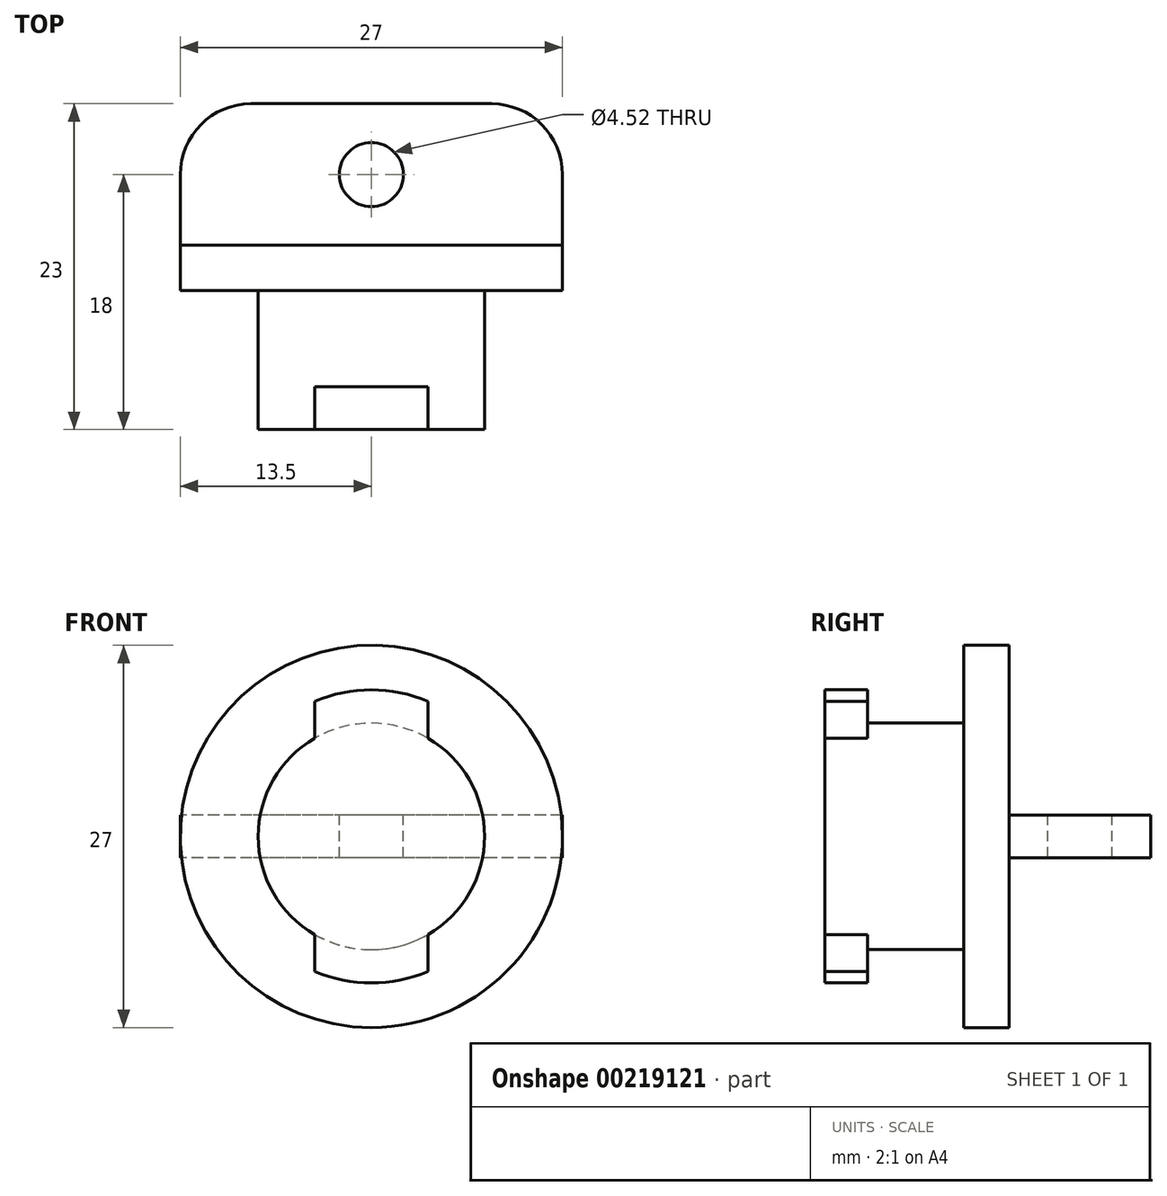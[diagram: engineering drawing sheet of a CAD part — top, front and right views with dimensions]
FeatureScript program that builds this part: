
annotation { "Feature Type Name" : "Feature", "Feature Type Description" : "" }
export const myFeature = defineFeature(function(context is Context, id is Id, definition is map)
    precondition{}
    {
        {
            var Q0;
            Q0=qCreatedBy(makeId("Front.planeOp"),FACE);
            var sketch = newSketch(context, id + "F0", { "sketchPlane" : qUnion([Q0])});
            skCircle(sketch, "E0", {"center": v(0, 0) * mm, "radius": 13.5 * mm});
            skCircle(sketch, "E1", {"center": v(0, 0) * mm, "radius": 8 * mm});
            skSolve(sketch);
        }
        {
            var Q0;
            Q0=makeQuery(id+"F0.imprint","IMPRINT",FACE,{"disambiguationData":[TD([[makeQuery(id+"F0.imprint","IMPRINT",EDGE,{"derivedFrom":sQuery(id+"F0.wireOp",EDGE,"E1")}),1.0]])]});
            extrude(context, id + "F1", {"entities" : qUnion([Q0]), "depth" : 13 * mm});
        }
        {
            var Q0;
            Q0=qSketchRegion(id+"F0",true);
            extrude(context, id + "F2", {"entities" : qUnion([Q0]), "operationType" : NewBodyOperationType.ADD, "depth" : 3.2 * mm});
        }
        {
            var Q0;
            Q0=makeQuery(id+"F2.opExtrude","CAP_FACE",FACE,{"disambiguationData":[OSD([sQuery(id+"F0.wireOp",EDGE,"E0"),sQuery(id+"F0.wireOp",EDGE,"E1")])],"isStart":false});
            cPlane(context, id + "F3", {"entities" : qUnion([Q0]), "cplaneType" : CPlaneType.OFFSET, "offset" : 6.8 * mm, "width" : 150 * mm, "height" : 150 * mm});
        }
        {
            var Q0;
            Q0=qCreatedBy(id+"F3.planeOp",FACE);
            var sketch = newSketch(context, id + "F4", { "sketchPlane" : qUnion([Q0])});
            skLineSegment(sketch, "E2.bottom", {"start": v(4, -10.35) * mm, "end": v(-4, -10.35) * mm});
            skLineSegment(sketch, "E2.top", {"start": v(4, 10.35) * mm, "end": v(-4, 10.35) * mm});
            skLineSegment(sketch, "E2.left", {"start": v(4, -10.35) * mm, "end": v(4, 10.35) * mm});
            skLineSegment(sketch, "E2.right", {"start": v(-4, -10.35) * mm, "end": v(-4, 10.35) * mm});
            skPoint(sketch, "E2.middle", {"position": v(0, 0) * mm});
            skCircle(sketch, "E3", {"center": v(0, 0) * mm, "radius": 10.35 * mm});
            skSolve(sketch);
        }
        {
            var Q0;
            {var subQ0=sQuery(id+"F4.wireOp",EDGE,"E3");var subQ5=sQuery(id+"F4.wireOp",EDGE,"E2.left");var subQ6=makeQuery(id+"F4.imprint","INTERSECT",VERTEX,{"disambiguationData":[OD(0.0)],"derivedFrom":[subQ5,subQ0]});Q0=makeQuery(id+"F4.imprint","IMPRINT",FACE,{"disambiguationData":[TD([[makeQuery(id+"F4.imprint","IMPRINT",EDGE,{"disambiguationData":[TD([[subQ6,-1.0]])],"derivedFrom":subQ5}),1.0]])]});}
            extrude(context, id + "F5", {"entities" : qUnion([Q0]), "operationType" : NewBodyOperationType.ADD, "depth" : 3 * mm});
        }
        {
            var Q0;
            Q0=qCreatedBy(makeId("Front.planeOp"),FACE);
            var sketch = newSketch(context, id + "F6", { "sketchPlane" : qUnion([Q0])});
            skLineSegment(sketch, "E4.bottom", {"start": v(13.5, -1.5) * mm, "end": v(-13.5, -1.5) * mm});
            skLineSegment(sketch, "E4.top", {"start": v(13.5, 1.5) * mm, "end": v(-13.5, 1.5) * mm});
            skLineSegment(sketch, "E4.left", {"start": v(13.5, -1.5) * mm, "end": v(13.5, 1.5) * mm});
            skLineSegment(sketch, "E4.right", {"start": v(-13.5, -1.5) * mm, "end": v(-13.5, 1.5) * mm});
            skPoint(sketch, "E4.middle", {"position": v(0, 0) * mm});
            skSolve(sketch);
        }
        {
            var Q0;
            Q0=makeQuery(id+"F6.imprint","IMPRINT",FACE,{"disambiguationData":[TD([[makeQuery(id+"F6.imprint","IMPRINT",EDGE,{"derivedFrom":sQuery(id+"F6.wireOp",EDGE,"E4.bottom")}),-1.0]])]});
            extrude(context, id + "F7", {"entities" : qUnion([Q0]), "operationType" : NewBodyOperationType.ADD, "oppositeDirection" : true, "depth" : 10 * mm});
        }
        {
            var Q0;
            Q0=makeQuery(id+"F7.opExtrude","CAP_EDGE",EDGE,{"disambiguationData":[OSD([sQuery(id+"F6.wireOp",EDGE,"E4.right")])],"isStart":false});
            fillet(context, id + "F8", {"entities" : qUnion([Q0]), "radius" : 5 * mm, "tangentPropagation" : true, "allowEdgeOverflow" : false});
        }
        {
            var Q0;
            Q0=makeQuery(id+"F7.opExtrude","CAP_EDGE",EDGE,{"disambiguationData":[OSD([sQuery(id+"F6.wireOp",EDGE,"E4.left")])],"isStart":false});
            fillet(context, id + "F9", {"entities" : qUnion([Q0]), "radius" : 5 * mm, "tangentPropagation" : true, "allowEdgeOverflow" : false});
        }
        {
            var Q0;
            Q0=makeQuery(id+"F7.opExtrude","SWEPT_FACE",FACE,{"disambiguationData":[OSD([sQuery(id+"F6.wireOp",EDGE,"E4.top")])]});
            var sketch = newSketch(context, id + "F10", { "sketchPlane" : qUnion([Q0])});
            skSolve(sketch);
        }
        {
            var Q0;
            {var subQ1=sQuery(id+"F6.wireOp",EDGE,"E4.top");Q0=makeQuery(id+"F10.imprint","IMPRINT",FACE,{"disambiguationData":[TD([[makeQuery(id+"F10.imprint","IMPRINT",EDGE,{"derivedFrom":makeQuery(id+"F7.opExtrude","CAP_EDGE",EDGE,{"disambiguationData":[OSD([subQ1])],"isStart":false})}),1.0]])]});}
            var sketch = newSketch(context, id + "F11", { "sketchPlane" : qUnion([Q0])});
            skCircle(sketch, "E5", {"center": v(0, 5) * mm, "radius": 2.26 * mm});
            skSolve(sketch);
        }
        {
            var Q0;
            Q0=makeQuery(id+"F11.imprint","IMPRINT",FACE,{"disambiguationData":[TD([[makeQuery(id+"F11.imprint","IMPRINT",EDGE,{"derivedFrom":sQuery(id+"F11.wireOp",EDGE,"E5")}),1.0]])]});
            extrude(context, id + "F12", {"entities" : qUnion([Q0]), "operationType" : NewBodyOperationType.REMOVE, "endBound" : BoundingType.UP_TO_NEXT, "oppositeDirection" : true, "depth" : 25 * mm});
        }
    });
